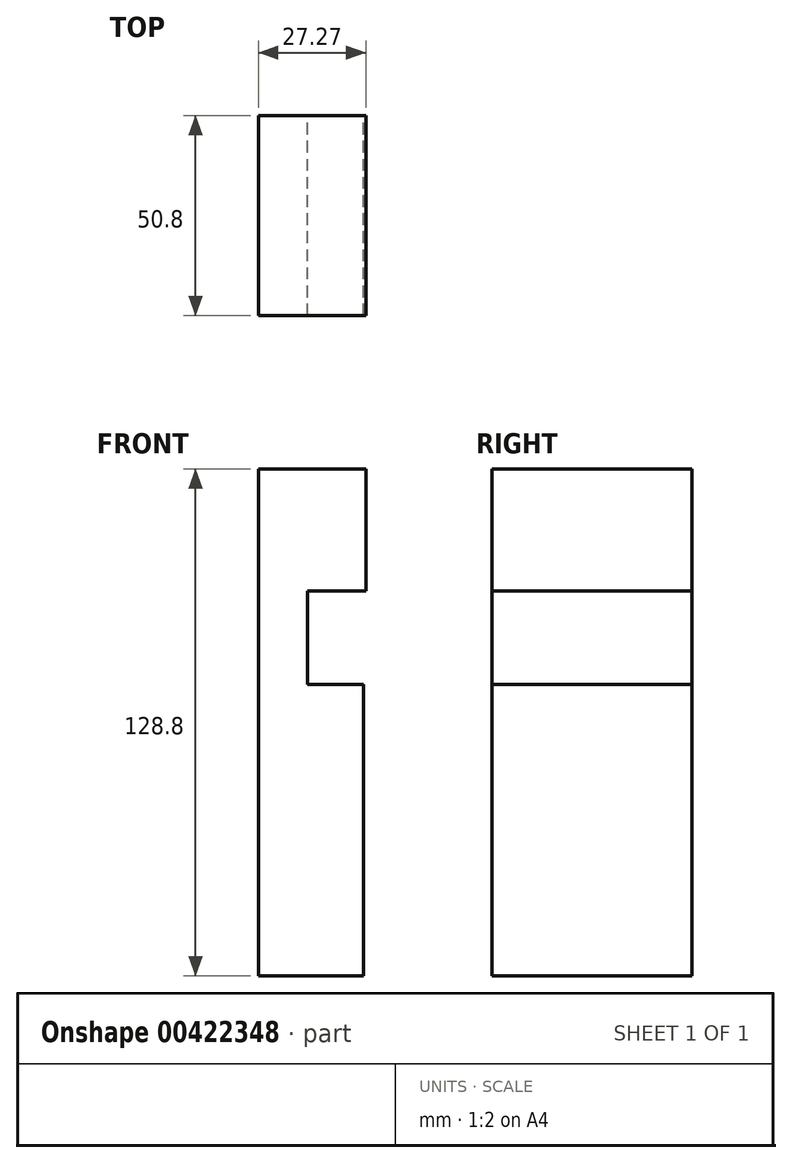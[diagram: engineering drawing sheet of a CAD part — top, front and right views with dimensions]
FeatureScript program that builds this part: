
annotation { "Feature Type Name" : "Feature", "Feature Type Description" : "" }
export const myFeature = defineFeature(function(context is Context, id is Id, definition is map)
    precondition{}
    {
        {
            var Q0;
            Q0=qCreatedBy(makeId("Front.planeOp"),FACE);
            var sketch = newSketch(context, id + "F0", { "sketchPlane" : qUnion([Q0])});
            skLineSegment(sketch, "E0", {"start": v(-35.36, 54.72) * mm, "end": v(-62.63, 54.72) * mm});
            skLineSegment(sketch, "E1", {"start": v(-62.63, 54.72) * mm, "end": v(-62.63, -74.08) * mm});
            skLineSegment(sketch, "E2", {"start": v(-62.63, -74.08) * mm, "end": v(-35.96, -74.08) * mm});
            skLineSegment(sketch, "E3", {"start": v(-35.96, -74.08) * mm, "end": v(-35.96, -14.22) * mm});
            skLineSegment(sketch, "E4", {"start": v(-35.36, 54.72) * mm, "end": v(-35.36, 23.7) * mm});
            skLineSegment(sketch, "E5", {"start": v(-35.36, 23.7) * mm, "end": v(-50.18, 23.7) * mm});
            skLineSegment(sketch, "E6", {"start": v(-35.96, -14.22) * mm, "end": v(-35.96, 0) * mm});
            skLineSegment(sketch, "E7", {"start": v(-35.96, 0) * mm, "end": v(-50.18, 0) * mm});
            skLineSegment(sketch, "E8", {"start": v(-50.18, 0) * mm, "end": v(-50.18, 23.7) * mm});
            skSolve(sketch);
        }
        {
            var Q0;
            Q0 = qSketchRegion(id + "F0", true);
            extrude(context, id + "F1", {"entities" : qUnion([Q0]), "depth" : 50.8 * mm});
        }
    });
